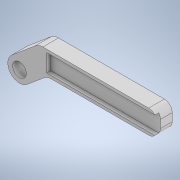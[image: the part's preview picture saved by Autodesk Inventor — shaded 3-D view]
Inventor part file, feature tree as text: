
AUTODESK INVENTOR PART (.ipt)
format: ipt  version: 2020 (Build 240168000, 168)  size: 130,560 bytes
history: native  units: mm
features: extrude x2, sketch x2
ambient origin geometry x8: Origin, YZ Plane, XZ Plane, XY Plane, X Axis, Y Axis, Z Axis, Center Point
bodies: Solid1 (feature_tree)
feature tree (4):
  extrude  "Extrusion1"  Depth=6.0mm
  extrude  "Extrusion2"  Depth=1.0mm
  sketch  "Sketch1"  dims[d0=6.0mm d1=6.0mm]
  sketch  "Sketch2"  dims[d2=3.0mm d3=24.43461mm d4=2.0mm d5=2.0mm d6=35.0mm d7=3.5mm d8=4.0mm d9=0.0mm d10=4.5mm d11=28.0mm d12=1.0mm d13=0.0mm]
